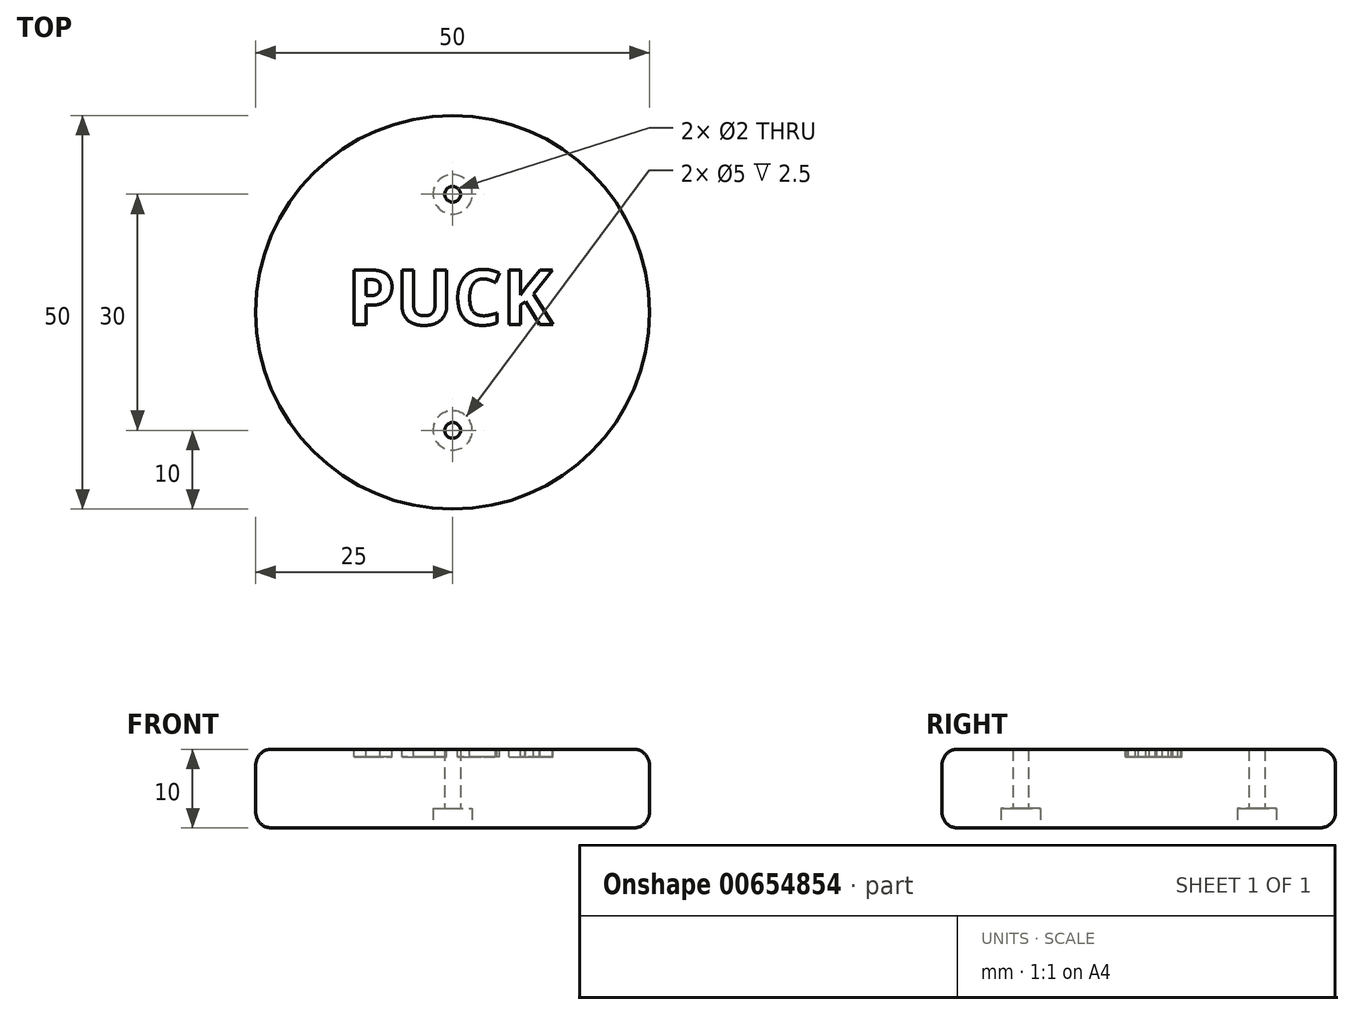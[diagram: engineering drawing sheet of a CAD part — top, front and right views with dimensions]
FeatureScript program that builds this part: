
annotation { "Feature Type Name" : "Feature", "Feature Type Description" : "" }
export const myFeature = defineFeature(function(context is Context, id is Id, definition is map)
    precondition{}
    {
        {
            var Q0;
            Q0=qCreatedBy(makeId("Top.planeOp"),FACE);
            var sketch = newSketch(context, id + "F0", { "sketchPlane" : qUnion([Q0])});
            skCircle(sketch, "E0", {"center": v(0, 0) * mm, "radius": 25 * mm});
            skSolve(sketch);
        }
        {
            var Q0;
            Q0=qSketchRegion(id+"F0",true);
            extrude(context, id + "F1", {"entities" : qUnion([Q0]), "depth" : 10 * mm});
        }
        {
            var Q0;
            Q0=makeQuery(id+"F1.opExtrude","CAP_FACE",FACE,{"disambiguationData":[OSD([sQuery(id+"F0.wireOp",EDGE,"E0")])],"isStart":false});
            var sketch = newSketch(context, id + "F2", { "sketchPlane" : qUnion([Q0])});
            skText(sketch, "E1", { "text": "PUCK", "fontName": "OpenSans-Bold.ttf"});
            const initialGuessF2  = {"E1": [-0.01337, -0.00157, 1, 0, 0.007]};
            skSetInitialGuess(sketch, initialGuessF2);
            skSolve(sketch);
        }
        {
            var Q0;
            Q0=qSketchRegion(id+"F2",true);
            extrude(context, id + "F3", {"entities" : qUnion([Q0]), "operationType" : NewBodyOperationType.REMOVE, "oppositeDirection" : true, "depth" : 1 * mm});
        }
        {
            var Q0;
            Q0=makeQuery(id+"F1.opExtrude","CAP_EDGE",EDGE,{"disambiguationData":[OSD([sQuery(id+"F0.wireOp",EDGE,"E0")])],"isStart":false});
            var Q1;
            Q1=makeQuery(id+"F1.opExtrude","CAP_EDGE",EDGE,{"disambiguationData":[OSD([sQuery(id+"F0.wireOp",EDGE,"E0")])],"isStart":true});
            fillet(context, id + "F4", {"entities" : qUnion([Q0, Q1]), "radius" : 2 * mm, "tangentPropagation" : true, "allowEdgeOverflow" : false});
        }
        {
            var Q0;
            Q0=makeQuery(id+"F1.opExtrude","CAP_FACE",FACE,{"disambiguationData":[OSD([sQuery(id+"F0.wireOp",EDGE,"E0")])],"isStart":true});
            var sketch = newSketch(context, id + "F5", { "sketchPlane" : qUnion([Q0])});
            skPoint(sketch, "E2", {"position": v(0, 15) * mm});
            skPoint(sketch, "E3", {"position": v(0, -15) * mm});
            skSolve(sketch);
        }
        {
            var Q0;
            Q0=sQuery(id+"F5.wireOp",VERTEX,"E2");
            var Q1;
            Q1=sQuery(id+"F5.wireOp",VERTEX,"E3");
            var Q2;
            Q2=makeQuery(id+"F1.opExtrude","SWEPT_BODY",BODY,{"disambiguationData":[OSD([sQuery(id+"F0.wireOp",EDGE,"E0")])]});
            hole(context, id + "F6", {"style" : HoleStyle.C_BORE, "endStyle" : HoleEndStyle.THROUGH, "holeDiameter" : 2 * mm, "cBoreDiameter" : 5 * mm, "cBoreDepth" : 2.5 * mm, "startFromSketch" : true, "locations" : qUnion([Q0, Q1]), "scope" : qUnion([Q2]), "isTappedThrough" : true});
        }
    });
